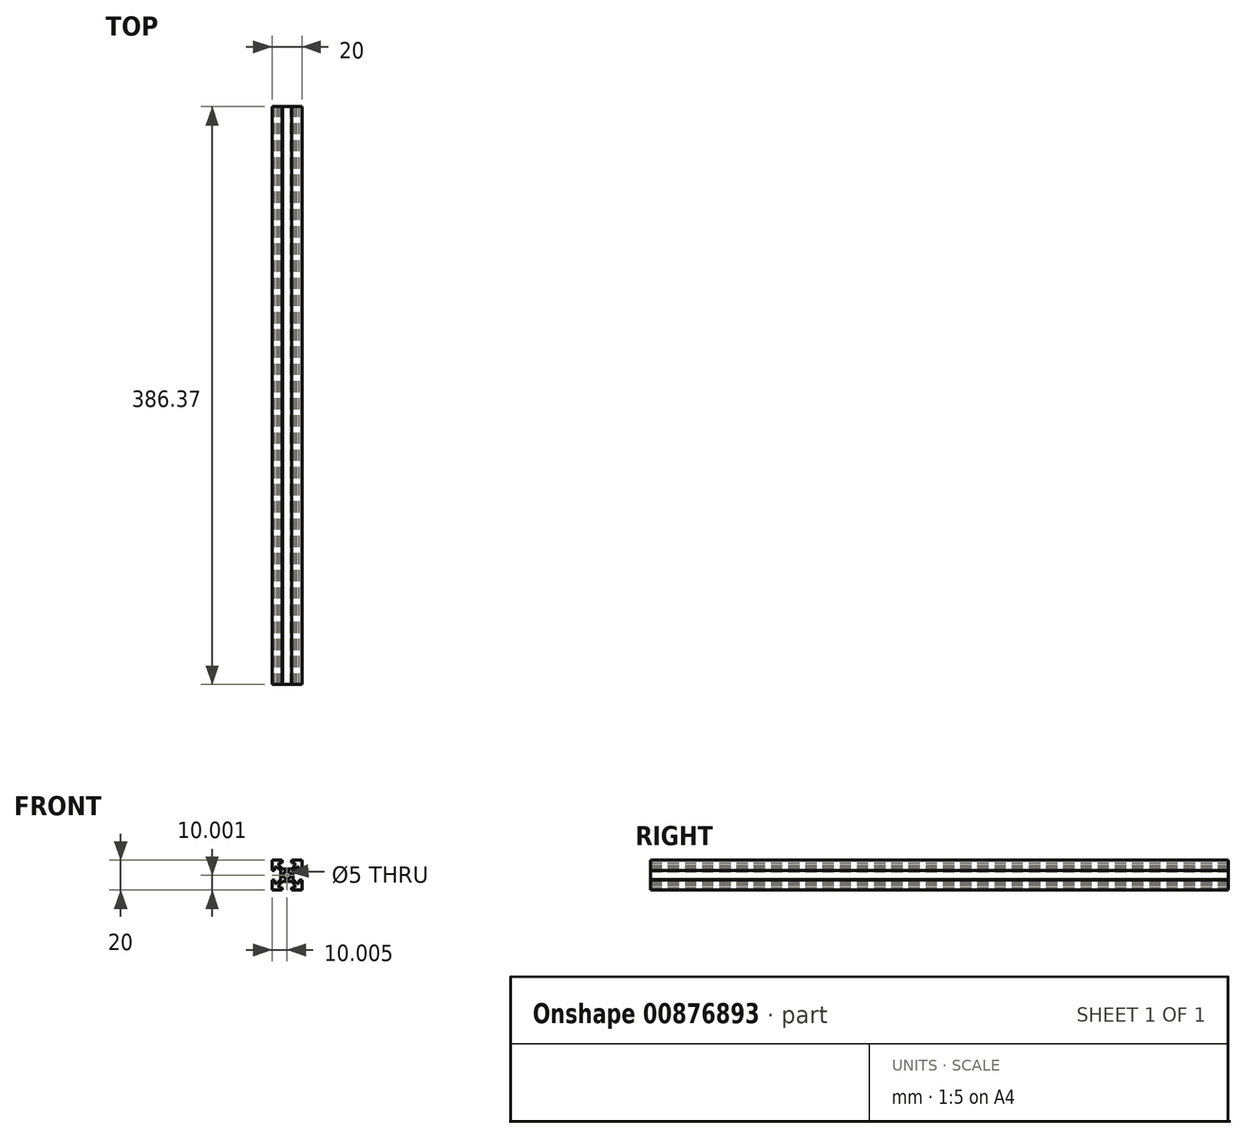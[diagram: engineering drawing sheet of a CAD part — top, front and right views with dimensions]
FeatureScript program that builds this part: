
annotation { "Feature Type Name" : "Feature", "Feature Type Description" : "" }
export const myFeature = defineFeature(function(context is Context, id is Id, definition is map)
    precondition{}
    {
        {
            var Q0;
            Q0=qCreatedBy(makeId("Front.planeOp"),FACE);
            var sketch = newSketch(context, id + "F0", { "sketchPlane" : qUnion([Q0])});
            skLineSegment(sketch, "E0.bottom", {"start": v(-26.43, 38.47) * mm, "end": v(-6.43, 38.47) * mm});
            skLineSegment(sketch, "E0.top", {"start": v(-26.43, 18.47) * mm, "end": v(-6.43, 18.47) * mm});
            skLineSegment(sketch, "E0.left", {"start": v(-26.43, 38.47) * mm, "end": v(-26.43, 18.47) * mm});
            skLineSegment(sketch, "E0.right", {"start": v(-6.43, 38.47) * mm, "end": v(-6.43, 18.47) * mm});
            skPoint(sketch, "E0.middle", {"position": v(-16.43, 28.47) * mm});
            skLineSegment(sketch, "E1", {"start": v(-8.23, 31.57) * mm, "end": v(-6.43, 31.57) * mm});
            skLineSegment(sketch, "E2.MirrorCS", {"start": v(-8.23, 25.37) * mm, "end": v(-6.43, 25.37) * mm});
            skLineSegment(sketch, "E3", {"start": v(-8.23, 31.57) * mm, "end": v(-8.23, 33.97) * mm});
            skLineSegment(sketch, "E4.MirrorCS", {"start": v(-8.23, 25.37) * mm, "end": v(-8.23, 22.97) * mm});
            skLineSegment(sketch, "E5", {"start": v(-8.23, 33.97) * mm, "end": v(-9.83, 33.97) * mm});
            skLineSegment(sketch, "E6.MirrorCS", {"start": v(-8.23, 22.97) * mm, "end": v(-9.83, 22.97) * mm});
            skCircle(sketch, "E7", {"center": v(-16.43, 28.47) * mm, "radius": 2.5 * mm});
            skLineSegment(sketch, "E8", {"start": v(-12.33, 31.47) * mm, "end": v(-12.33, 25.47) * mm});
            skLineSegment(sketch, "E9", {"start": v(-12.33, 31.47) * mm, "end": v(-9.83, 33.97) * mm});
            skLineSegment(sketch, "E10.MirrorCS", {"start": v(-12.33, 25.47) * mm, "end": v(-9.83, 22.97) * mm});
            skLineSegment(sketch, "E11.MirrorCS", {"start": v(-24.63, 31.57) * mm, "end": v(-26.43, 31.57) * mm});
            skLineSegment(sketch, "E12.MirrorCS", {"start": v(-24.63, 31.57) * mm, "end": v(-24.63, 33.97) * mm});
            skLineSegment(sketch, "E13.MirrorCS", {"start": v(-24.63, 33.97) * mm, "end": v(-23.03, 33.97) * mm});
            skLineSegment(sketch, "E14.MirrorCS", {"start": v(-20.53, 31.47) * mm, "end": v(-23.03, 33.97) * mm});
            skLineSegment(sketch, "E15.MirrorCS", {"start": v(-20.53, 31.47) * mm, "end": v(-20.53, 25.47) * mm});
            skLineSegment(sketch, "E16.MirrorCS", {"start": v(-20.53, 25.47) * mm, "end": v(-23.03, 22.97) * mm});
            skLineSegment(sketch, "E17.MirrorCS", {"start": v(-24.63, 22.97) * mm, "end": v(-23.03, 22.97) * mm});
            skLineSegment(sketch, "E18.MirrorCS", {"start": v(-24.63, 25.37) * mm, "end": v(-24.63, 22.97) * mm});
            skLineSegment(sketch, "E19.MirrorCS", {"start": v(-24.63, 25.37) * mm, "end": v(-26.43, 25.37) * mm});
            skLineSegment(sketch, "E20", {"start": v(-19.53, 38.47) * mm, "end": v(-19.53, 36.67) * mm});
            skLineSegment(sketch, "E21", {"start": v(-19.53, 36.67) * mm, "end": v(-21.93, 36.67) * mm});
            skLineSegment(sketch, "E22", {"start": v(-21.93, 36.67) * mm, "end": v(-21.93, 35.07) * mm});
            skLineSegment(sketch, "E23", {"start": v(-19.43, 32.57) * mm, "end": v(-16.43, 32.57) * mm});
            skLineSegment(sketch, "E24.MirrorCS", {"start": v(-13.33, 38.47) * mm, "end": v(-13.33, 36.67) * mm});
            skLineSegment(sketch, "E25.MirrorCS", {"start": v(-13.33, 36.67) * mm, "end": v(-10.93, 36.67) * mm});
            skLineSegment(sketch, "E26.MirrorCS", {"start": v(-10.93, 36.67) * mm, "end": v(-10.93, 35.07) * mm});
            skLineSegment(sketch, "E27.MirrorCS", {"start": v(-13.43, 32.57) * mm, "end": v(-16.43, 32.57) * mm});
            skLineSegment(sketch, "E28", {"start": v(-10.93, 35.07) * mm, "end": v(-13.43, 32.57) * mm});
            skLineSegment(sketch, "E29", {"start": v(-21.93, 35.07) * mm, "end": v(-19.43, 32.57) * mm});
            skLineSegment(sketch, "E30.MirrorCS", {"start": v(-19.53, 18.47) * mm, "end": v(-19.53, 20.27) * mm});
            skLineSegment(sketch, "E31.MirrorCS", {"start": v(-19.53, 20.27) * mm, "end": v(-21.93, 20.27) * mm});
            skLineSegment(sketch, "E32.MirrorCS", {"start": v(-21.93, 20.27) * mm, "end": v(-21.93, 21.87) * mm});
            skLineSegment(sketch, "E33.MirrorCS", {"start": v(-21.93, 21.87) * mm, "end": v(-19.43, 24.37) * mm});
            skLineSegment(sketch, "E34.MirrorCS", {"start": v(-13.33, 18.47) * mm, "end": v(-13.33, 20.27) * mm});
            skLineSegment(sketch, "E35.MirrorCS", {"start": v(-13.33, 20.27) * mm, "end": v(-10.93, 20.27) * mm});
            skLineSegment(sketch, "E36.MirrorCS", {"start": v(-10.93, 20.27) * mm, "end": v(-10.93, 21.87) * mm});
            skLineSegment(sketch, "E37.MirrorCS", {"start": v(-10.93, 21.87) * mm, "end": v(-13.43, 24.37) * mm});
            skLineSegment(sketch, "E38.MirrorCS", {"start": v(-13.43, 24.37) * mm, "end": v(-16.43, 24.37) * mm});
            skLineSegment(sketch, "E39.MirrorCS", {"start": v(-19.43, 24.37) * mm, "end": v(-16.43, 24.37) * mm});
            skSolve(sketch);
        }
        {
            var Q0;
            {var subQ5=sQuery(id+"F0.wireOp",EDGE,"E1");Q0=makeQuery(id+"F0.imprint","IMPRINT",FACE,{"disambiguationData":[TD([[makeQuery(id+"F0.imprint","IMPRINT",EDGE,{"derivedFrom":subQ5}),1.0]])]});}
            extrude(context, id + "F1", {"entities" : qUnion([Q0]), "depth" : 386.37 * mm, "offsetDistance" : 25 * mm});
        }
    });
